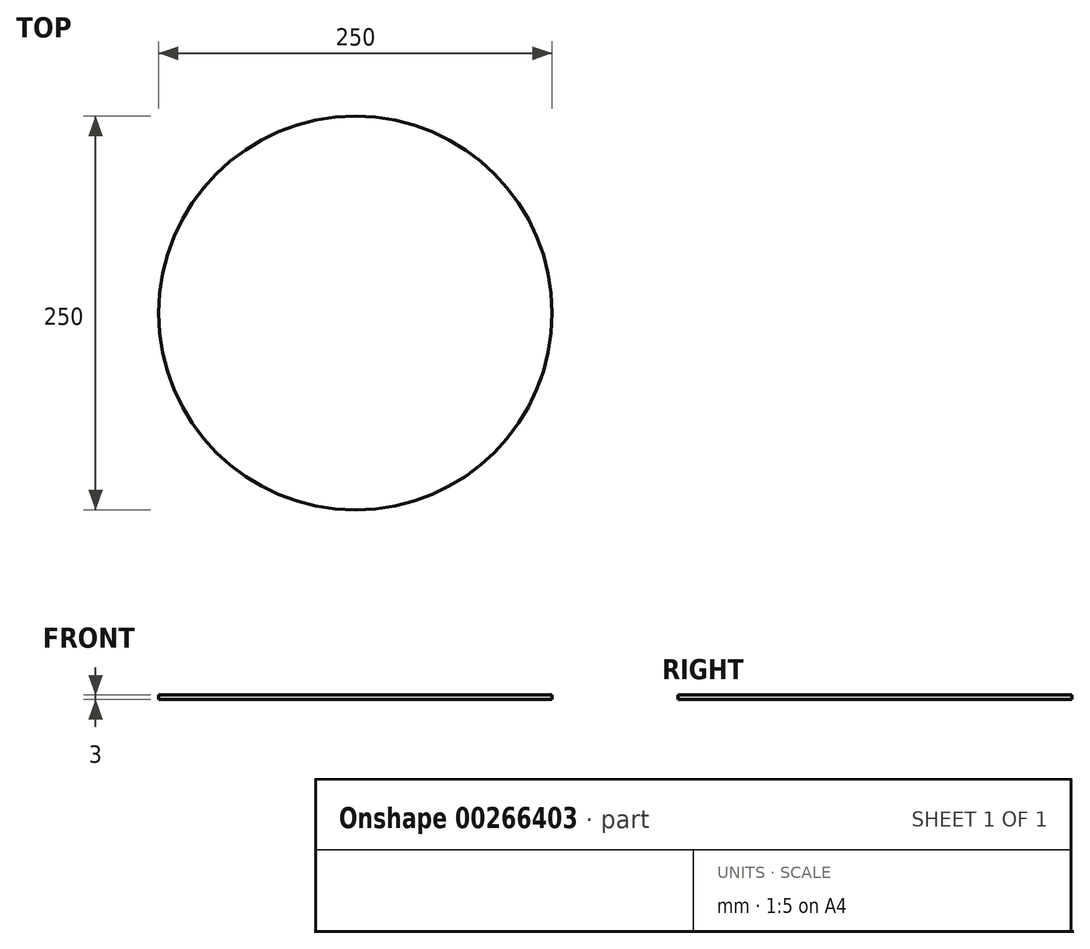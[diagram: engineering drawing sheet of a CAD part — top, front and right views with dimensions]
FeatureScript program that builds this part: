
annotation { "Feature Type Name" : "Feature", "Feature Type Description" : "" }
export const myFeature = defineFeature(function(context is Context, id is Id, definition is map)
    precondition{}
    {
        {
            var Q0;
            Q0=qCreatedBy(makeId("Top.planeOp"),FACE);
            var sketch = newSketch(context, id + "F0", { "sketchPlane" : qUnion([Q0])});
            skCircle(sketch, "E0", {"center": v(0, 0) * mm, "radius": 125 * mm});
            skSolve(sketch);
        }
        {
            var Q0;
            Q0=makeQuery(id+"F0.imprint","IMPRINT",FACE,{"disambiguationData":[TD([[makeQuery(id+"F0.imprint","IMPRINT",EDGE,{"derivedFrom":sQuery(id+"F0.wireOp",EDGE,"E0")}),1.0]])]});
            extrude(context, id + "F1", {"entities" : qUnion([Q0]), "depth" : 3 * mm, "offsetDistance" : 25 * mm});
        }
    });
